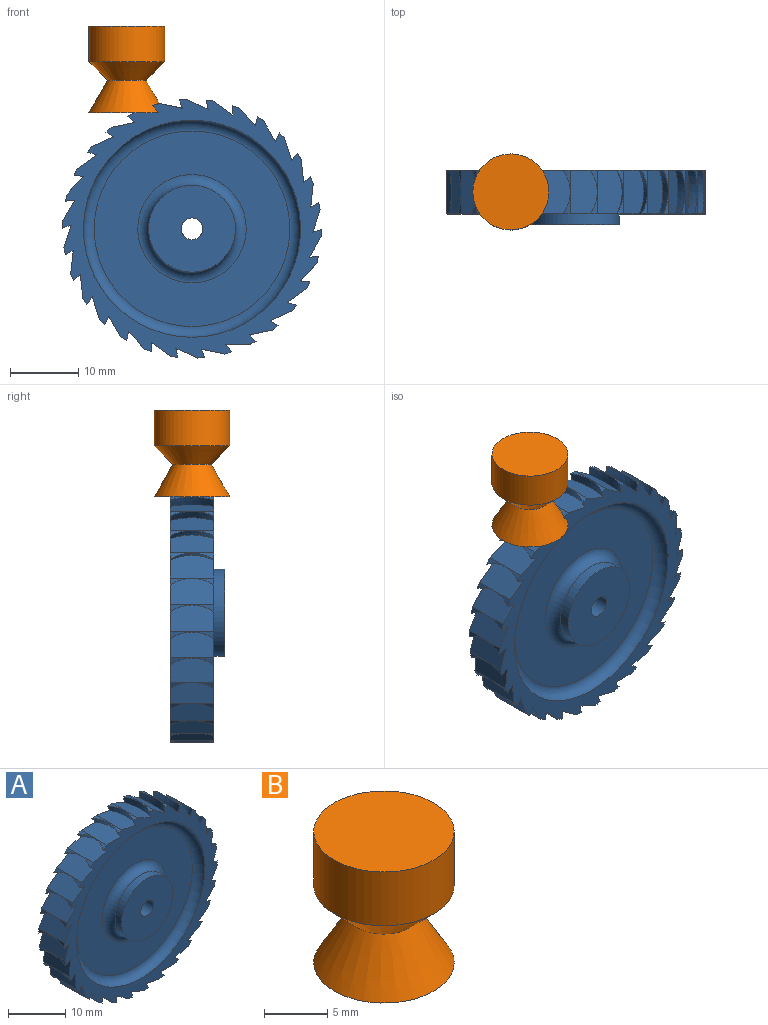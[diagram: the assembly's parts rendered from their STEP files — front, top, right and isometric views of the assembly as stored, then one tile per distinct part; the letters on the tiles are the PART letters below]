
ASSEMBLY  parts=2 mates=1
PART A: 105 faces, bbox 38.5x9.1x38.3 mm
  f0: cylinder r=18.92mm len=6.35mm, axis (0,-1,0), area 2.3mm2, adj f1,f95,f97,f104
  f1: plane 6.35x4.37mm, normal (0.21,0,0.98), area 26.3mm2, adj f0,f2,f95,f97
  f2: cone r=1.59mm half-angle=30deg, axis (-0.21,0,-0.98), area 10.1mm2, adj f1,f3,f95,f97
  f3: cylinder r=18.92mm len=6.35mm, axis (0,-1,0), area 2.3mm2, adj f2,f4,f95,f97
  f4: plane 6.35x4.08mm, normal (0.41,0,0.91), area 26.3mm2, adj f3,f5,f95,f97
  f5: cone r=1.59mm half-angle=30deg, axis (-0.41,0,-0.91), area 10.1mm2, adj f4,f6,f95,f97
  f6: cylinder r=18.92mm len=6.35mm, axis (0,-1,0), area 2.3mm2, adj f5,f7,f95,f97
  f7: plane 6.35x3.61mm, normal (0.59,0,0.81), area 26.3mm2, adj f6,f8,f95,f97
  f8: cone r=1.59mm half-angle=30deg, axis (-0.59,0,-0.81), area 10.1mm2, adj f7,f9,f95,f97
  f9: cylinder r=18.92mm len=6.35mm, axis (0,-1,0), area 2.3mm2, adj f8,f10,f95,f97
  f10: plane 6.35x3.32mm, normal (0.74,0,0.67), area 26.3mm2, adj f9,f11,f95,f97
  f11: cone r=1.59mm half-angle=30deg, axis (-0.74,0,-0.67), area 10.1mm2, adj f10,f12,f95,f97
  f12: cylinder r=18.92mm len=6.35mm, axis (0,-1,0), area 2.3mm2, adj f11,f13,f95,f97
  f13: plane 6.35x3.87mm, normal (0.87,0,0.5), area 26.3mm2, adj f12,f14,f95,f97
  f14: cone r=1.59mm half-angle=30deg, axis (-0.87,0,-0.5), area 10.1mm2, adj f13,f15,f95,f97
  f15: cylinder r=18.92mm len=6.35mm, axis (0,-1,0), area 2.3mm2, adj f14,f16,f95,f97
  f16: plane 6.35x4.25mm, normal (0.95,0,0.31), area 26.3mm2, adj f15,f17,f95,f97
  f17: cone r=1.59mm half-angle=30deg, axis (-0.95,0,-0.31), area 10.1mm2, adj f16,f18,f95,f97
  f18: cylinder r=18.92mm len=6.35mm, axis (0,-1,0), area 2.3mm2, adj f17,f19,f95,f97
  f19: plane 6.35x4.44mm, normal (0.99,0,0.1), area 26.3mm2, adj f18,f20,f95,f97
  f20: cone r=1.59mm half-angle=30deg, axis (-0.99,0,-0.1), area 10.1mm2, adj f19,f21,f95,f97
  f21: cylinder r=18.92mm len=6.35mm, axis (0,-1,0), area 2.3mm2, adj f20,f22,f95,f97
  f22: plane 6.35x4.44mm, normal (0.99,0,-0.1), area 26.3mm2, adj f21,f23,f95,f97
  f23: cone r=1.59mm half-angle=30deg, axis (-0.99,0,0.1), area 10.1mm2, adj f22,f24,f95,f97
  f24: cylinder r=18.92mm len=6.35mm, axis (0,-1,0), area 2.3mm2, adj f23,f25,f95,f97
  f25: plane 6.35x4.25mm, normal (0.95,0,-0.31), area 26.3mm2, adj f24,f26,f95,f97
  f26: cone r=1.59mm half-angle=30deg, axis (-0.95,0,0.31), area 10.1mm2, adj f25,f27,f95,f97
  f27: cylinder r=18.92mm len=6.35mm, axis (0,-1,0), area 2.3mm2, adj f26,f28,f95,f97
  f28: plane 6.35x3.87mm, normal (0.87,0,-0.5), area 26.3mm2, adj f27,f29,f95,f97
  f29: cone r=1.59mm half-angle=30deg, axis (-0.87,0,0.5), area 10.1mm2, adj f28,f30,f95,f97
  f30: cylinder r=18.92mm len=6.35mm, axis (0,-1,0), area 2.3mm2, adj f29,f31,f95,f97
  f31: plane 6.35x3.32mm, normal (0.74,0,-0.67), area 26.3mm2, adj f30,f32,f95,f97
  f32: cone r=1.59mm half-angle=30deg, axis (-0.74,0,0.67), area 10.1mm2, adj f31,f33,f95,f97
  f33: cylinder r=18.92mm len=6.35mm, axis (0,-1,0), area 2.3mm2, adj f32,f34,f95,f97
  f34: plane 6.35x3.61mm, normal (0.59,0,-0.81), area 26.3mm2, adj f33,f35,f95,f97
  f35: cone r=1.59mm half-angle=30deg, axis (-0.59,0,0.81), area 10.1mm2, adj f34,f36,f95,f97
  f36: cylinder r=18.92mm len=6.35mm, axis (0,-1,0), area 2.3mm2, adj f35,f37,f95,f97
  f37: plane 6.35x4.08mm, normal (0.41,0,-0.91), area 26.3mm2, adj f36,f38,f95,f97
  f38: cone r=1.59mm half-angle=30deg, axis (-0.41,0,0.91), area 10.1mm2, adj f37,f39,f95,f97
  f39: cylinder r=18.92mm len=6.35mm, axis (0,-1,0), area 2.3mm2, adj f38,f40,f95,f97
  f40: plane 6.35x4.37mm, normal (0.21,0,-0.98), area 26.3mm2, adj f39,f41,f95,f97
  f41: cone r=1.59mm half-angle=30deg, axis (-0.21,0,0.98), area 10.1mm2, adj f40,f42,f95,f97
  f42: cylinder r=18.92mm len=6.35mm, axis (0,-1,0), area 2.3mm2, adj f41,f43,f95,f97
  f43: plane 6.35x4.47mm, normal (0,0,-1), area 26.3mm2, adj f42,f44,f95,f97
  f44: cone r=1.59mm half-angle=30deg, axis (0,0,1), area 10.1mm2, adj f43,f45,f95,f97
  f45: cylinder r=18.92mm len=6.35mm, axis (0,-1,0), area 2.3mm2, adj f44,f46,f95,f97
  f46: plane 6.35x4.37mm, normal (-0.21,0,-0.98), area 26.3mm2, adj f45,f47,f95,f97
  f47: cone r=1.59mm half-angle=30deg, axis (0.21,0,0.98), area 10.1mm2, adj f46,f48,f95,f97
  f48: cylinder r=18.92mm len=6.35mm, axis (0,-1,0), area 2.3mm2, adj f47,f49,f95,f97
  f49: plane 6.35x4.08mm, normal (-0.41,0,-0.91), area 26.3mm2, adj f48,f50,f95,f97
  f50: cone r=1.59mm half-angle=30deg, axis (0.41,0,0.91), area 10.1mm2, adj f49,f51,f95,f97
  f51: cylinder r=18.92mm len=6.35mm, axis (0,-1,0), area 2.3mm2, adj f50,f52,f95,f97
  f52: plane 6.35x3.61mm, normal (-0.59,0,-0.81), area 26.3mm2, adj f51,f53,f95,f97
  f53: cone r=1.59mm half-angle=30deg, axis (0.59,0,0.81), area 10.1mm2, adj f52,f54,f95,f97
  f54: cylinder r=18.92mm len=6.35mm, axis (0,-1,0), area 2.3mm2, adj f53,f55,f95,f97
  f55: plane 6.35x3.32mm, normal (-0.74,0,-0.67), area 26.3mm2, adj f54,f56,f95,f97
  f56: cone r=1.59mm half-angle=30deg, axis (0.74,0,0.67), area 10.1mm2, adj f55,f57,f95,f97
  f57: cylinder r=18.92mm len=6.35mm, axis (0,-1,0), area 2.3mm2, adj f56,f58,f95,f97
  f58: plane 6.35x3.87mm, normal (-0.87,0,-0.5), area 26.3mm2, adj f57,f59,f95,f97
  f59: cone r=1.59mm half-angle=30deg, axis (0.87,0,0.5), area 10.1mm2, adj f58,f60,f95,f97
  f60: cylinder r=18.92mm len=6.35mm, axis (0,-1,0), area 2.3mm2, adj f59,f61,f95,f97
  f61: plane 6.35x4.25mm, normal (-0.95,0,-0.31), area 26.3mm2, adj f60,f62,f95,f97
  f62: cone r=1.59mm half-angle=30deg, axis (0.95,0,0.31), area 10.1mm2, adj f61,f63,f95,f97
  f63: cylinder r=18.92mm len=6.35mm, axis (0,-1,0), area 2.3mm2, adj f62,f64,f95,f97
  f64: plane 6.35x4.44mm, normal (-0.99,0,-0.1), area 26.3mm2, adj f63,f65,f95,f97
  f65: cone r=1.59mm half-angle=30deg, axis (0.99,0,0.1), area 10.1mm2, adj f64,f66,f95,f97
  f66: cylinder r=18.92mm len=6.35mm, axis (0,-1,0), area 2.3mm2, adj f65,f67,f95,f97
  f67: plane 6.35x4.44mm, normal (-0.99,0,0.1), area 26.3mm2, adj f66,f68,f95,f97
  f68: cone r=1.59mm half-angle=30deg, axis (0.99,0,-0.1), area 10.1mm2, adj f67,f69,f95,f97
  f69: cylinder r=18.92mm len=6.35mm, axis (0,-1,0), area 2.3mm2, adj f68,f70,f95,f97
  f70: plane 6.35x4.25mm, normal (-0.95,0,0.31), area 26.3mm2, adj f69,f71,f95,f97
  f71: cone r=1.59mm half-angle=30deg, axis (0.95,0,-0.31), area 10.1mm2, adj f70,f72,f95,f97
  f72: cylinder r=18.92mm len=6.35mm, axis (0,-1,0), area 2.3mm2, adj f71,f73,f95,f97
  f73: plane 6.35x3.87mm, normal (-0.87,0,0.5), area 26.3mm2, adj f72,f74,f95,f97
  f74: cone r=1.59mm half-angle=30deg, axis (0.87,0,-0.5), area 10.1mm2, adj f73,f75,f95,f97
  f75: cylinder r=18.92mm len=6.35mm, axis (0,-1,0), area 2.3mm2, adj f74,f76,f95,f97
  f76: plane 6.35x3.32mm, normal (-0.74,0,0.67), area 26.3mm2, adj f75,f77,f95,f97
  f77: cone r=1.59mm half-angle=30deg, axis (0.74,0,-0.67), area 10.1mm2, adj f76,f78,f95,f97
  f78: cylinder r=18.92mm len=6.35mm, axis (0,-1,0), area 2.3mm2, adj f77,f79,f95,f97
  f79: plane 6.35x3.61mm, normal (-0.59,0,0.81), area 26.3mm2, adj f78,f80,f95,f97
  f80: cone r=1.59mm half-angle=30deg, axis (0.59,0,-0.81), area 10.1mm2, adj f79,f81,f95,f97
  f81: cylinder r=18.92mm len=6.35mm, axis (0,-1,0), area 2.3mm2, adj f80,f82,f95,f97
  f82: plane 6.35x4.08mm, normal (-0.41,0,0.91), area 26.3mm2, adj f81,f83,f95,f97
  f83: cone r=1.59mm half-angle=30deg, axis (0.41,0,-0.91), area 10.1mm2, adj f82,f84,f95,f97
  f84: cylinder r=18.92mm len=6.35mm, axis (0,-1,0), area 2.3mm2, adj f83,f85,f95,f97
  f85: plane 6.35x4.37mm, normal (-0.21,0,0.98), area 26.3mm2, adj f84,f86,f95,f97
  f86: cone r=1.59mm half-angle=30deg, axis (0.21,0,-0.98), area 10.1mm2, adj f85,f95,f96,f97
  f87: cylinder r=6.35mm len=12.7mm, axis (0,-1,0), area 63.8mm2, adj f88,f101
  f88: plane 12.7x12.7mm, normal (0,-1,0), area 118.8mm2, adj f87,f102
  f89: plane 12.7x12.7mm, normal (0,1,0), area 118.8mm2, adj f90,f102
  f90: cylinder r=6.35mm len=12.7mm, axis (0,-1,0), area 0.5mm2, adj f89,f91
  f91: torus R=7.92mm, axis (0,-1,0), area 107.6mm2, adj f90,f92
  f92: plane 28.6x28.6mm, normal (0,1,0), area 445.1mm2, adj f91,f93
  f93: torus R=14.3mm, axis (0,-1,0), area 237.8mm2, adj f92,f94
  f94: cylinder r=15.88mm len=31.75mm, axis (0,-1,0), area 1.3mm2, adj f93,f95
  f95: plane 37.88x37.85mm, normal (0,1,0), area 273.2mm2, adj f0,f1,f2,f3,f4,f5,f6,f7
  f96: cylinder r=18.92mm len=6.35mm, axis (0,-1,0), area 2.3mm2, adj f86,f95,f97,f103
  f97: plane 37.88x37.85mm, normal (0,-1,0), area 273.2mm2, adj f0,f1,f2,f3,f4,f5,f6,f7
  f98: cylinder r=15.88mm len=31.75mm, axis (0,-1,0), area 1.3mm2, adj f97,f99
  f99: torus R=14.3mm, axis (0,-1,0), area 237.8mm2, adj f98,f100
  f100: plane 28.6x28.6mm, normal (0,-1,0), area 445.1mm2, adj f99,f101
  f101: torus R=7.92mm, axis (0,-1,0), area 107.6mm2, adj f87,f100
  f102: cylinder r=1.59mm len=7.94mm, axis (0,-1,0), area 79.2mm2, adj f88,f89
  f103: plane 6.35x4.47mm, normal (0,0,1), area 26.3mm2, adj f95,f96,f97,f104
  f104: cone r=1.59mm half-angle=30deg, axis (0,0,-1), area 10.1mm2, adj f0,f95,f97,f103
PART B: 5 faces, bbox 11.1x11.1x12.7 mm
  f0: plane 11.11x11.11mm, normal (0,0,-1), area 97mm2, adj f1
  f1: cone r=2.81mm half-angle=30deg, axis (0,0,-1), area 144.2mm2, adj f0,f2
  f2: cone r=5.56mm half-angle=45deg, axis (0,0,1), area 102mm2, adj f1,f3
  f3: cylinder r=5.56mm len=11.11mm, axis (0,0,-1), area 181.8mm2, adj f2,f4
  f4: plane 11.11x11.11mm, normal (0,0,1), area 97mm2, adj f3
PLACE A t=(0,4.76,0)mm
PLACE B t=(-9.53,4.76,16.94)mm
MATE fastened A.f104 <-> B.f1  axis (0,0,1) through (-9.53,4.76,16.94)mm
